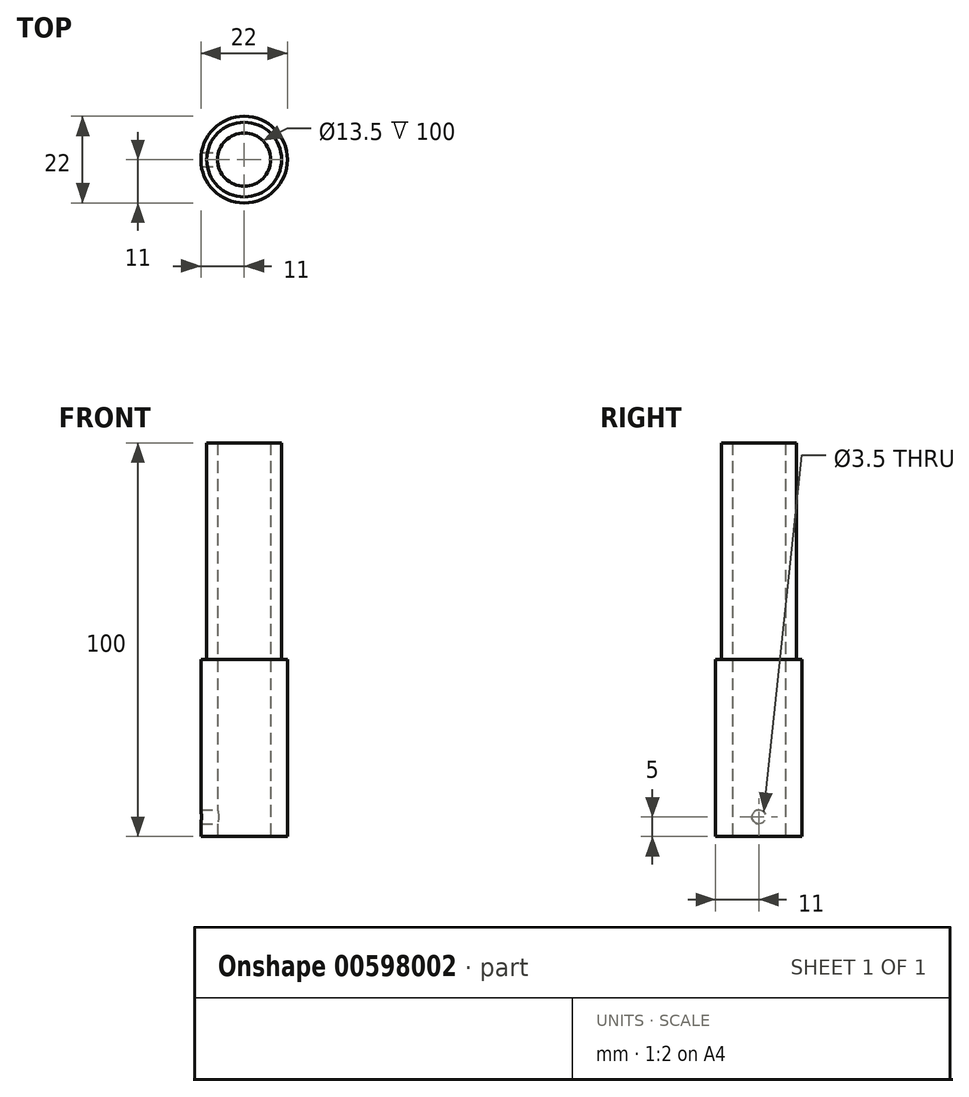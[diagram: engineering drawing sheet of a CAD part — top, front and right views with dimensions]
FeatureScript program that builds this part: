
annotation { "Feature Type Name" : "Feature", "Feature Type Description" : "" }
export const myFeature = defineFeature(function(context is Context, id is Id, definition is map)
    precondition{}
    {
        {
            var Q0;
            Q0=qCreatedBy(makeId("Top.planeOp"),FACE);
            var sketch = newSketch(context, id + "F0", { "sketchPlane" : qUnion([Q0])});
            skCircle(sketch, "E0", {"center": v(0, 0) * mm, "radius": 11 * mm});
            skCircle(sketch, "E1", {"center": v(0, 0) * mm, "radius": 6.75 * mm});
            skSolve(sketch);
        }
        {
            var Q0;
            Q0 = qSketchRegion(id + "F0", true);
            extrude(context, id + "F1", {"entities" : qUnion([Q0]), "depth" : 45 * mm, "offsetDistance" : 25 * mm});
        }
        {
            var Q0;
            Q0=makeQuery(id+"F1.opExtrude","CAP_FACE",FACE,{"disambiguationData":[OSD([sQuery(id+"F0.wireOp",EDGE,"E0"),sQuery(id+"F0.wireOp",EDGE,"E1")])],"isStart":false});
            var sketch = newSketch(context, id + "F2", { "sketchPlane" : qUnion([Q0])});
            skCircle(sketch, "E2", {"center": v(0, 0) * mm, "radius": 6.75 * mm});
            skCircle(sketch, "E3", {"center": v(0, 0) * mm, "radius": 9.5 * mm});
            skSolve(sketch);
        }
        {
            var Q0;
            Q0 = qSketchRegion(id + "F2", true);
            extrude(context, id + "F3", {"entities" : qUnion([Q0]), "operationType" : NewBodyOperationType.ADD, "depth" : 55 * mm, "offsetDistance" : 25 * mm});
        }
        {
            var Q0;
            Q0=qCreatedBy(makeId("Right.planeOp"),FACE);
            var sketch = newSketch(context, id + "F4", { "sketchPlane" : qUnion([Q0])});
            skLineSegment(sketch, "E4", {"start": v(0, 0) * mm, "end": v(0, 5) * mm});
            skCircle(sketch, "E5", {"center": v(0, 5) * mm, "radius": 1.75 * mm});
            skSolve(sketch);
        }
        {
            var Q0;
            Q0 = qSketchRegion(id + "F4", true);
            var Q1;
            Q1=makeQuery(id+"F1.opExtrude","SWEPT_FACE",FACE,{"disambiguationData":[OSD([sQuery(id+"F0.wireOp",EDGE,"E0")])]});
            extrude(context, id + "F5", {"entities" : qUnion([Q0]), "operationType" : NewBodyOperationType.REMOVE, "endBound" : BoundingType.UP_TO_SURFACE, "oppositeDirection" : true, "depth" : 25 * mm, "endBoundEntityFace" : qUnion([Q1]), "offsetDistance" : 25 * mm});
        }
    });
